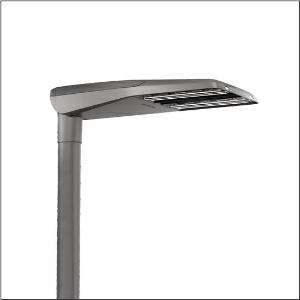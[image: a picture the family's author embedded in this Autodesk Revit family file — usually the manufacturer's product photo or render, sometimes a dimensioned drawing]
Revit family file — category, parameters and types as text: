
# Revit family: streetlight_sl_11_iq_midi___st1_0a_5xc3m41f08le_9450
name_source: partatom
category: Lighting Fixtures
units: mm (PartAtom-declared; Revit-internal decimal feet)

## family parameters
Cut with Voids When Loaded = No
Host = Face
Light Source = No
Part Type = Normal
Room Calculation Point = No
Round Connector Dimension = Use Diameter
Shared = No

## types (1)
- --- (1 x LED, 9290 lm, 60.4 W, 4000K)
    Apparent Load = 60 VA
    CIE Flux Codes = 33 66 96 100 100
    Color Rendering = 70
    Color Temperature = 4000K
    Default Elevation = 1800 mm
    Description = Streetlight SL 11 iQ midi, mast luminaire, primary light control with 3 zone facetted reflector, of plastic, silver coated, highly specular, primary optical cover: cover, of PMMA, transparent, light distribution: ST1.0a, light emission: direct distribution, primary light characteristic: asymmetric, installation type: post-top, side-entry, LED, High Power LED, rated luminous flux: 9.290lm, luminous efficacy: 154lm/W, light colour: 740, colour temperature: 4000K, control: optimised constant luminous flux control (CLO 2.0), Street-Remote, Desk-Remote (wireless, voltage-free reading and setting of iQ features in the workshop via application-optimized NFC function/RFID function), Light-Fading, Smart-Wire, Night-Set, Lumen-Switch, Temp-Guard, Auto-Match, with cable H07RN-F 5x 1.5mm², mains connection: 230..240V, AC, 50/60Hz, connection cable pre-assembled, cable length: 8,5m, start of lifetime: 60W, end of service life: 63W, reduction: 30W, luminaire housing, of diecast aluminium, powder-coated, Siteco® metallic grey (DB 702S), please order mast flange separately, inclination adjustable without tools: 0°, 5°, 10°, 15° (post-top) | 0°, -5°, -10°, -15° (side-entry), sealing non-destructively replaceable, multi-level sealing system, length: 780mm, width: 376mm, height: 118mm, mast flange for spigot size: 42mm (side-entry): 5XC10008XM4, 60/48mm (side-entry/post-top): 5XC10108XM2, 76/60mm (side-entry/post-top): 5XC10108XM1, equipment: standard, protection rating (complete): IP66, insulation class (complete): insulation class II (safety insulation), certification: CE, ENEC, VDE, impact resistance: IK09, permissible operating ambient temperature for outdoor applications: -25..+50°C, standard-compliant lighting for roads and squares, Environmental Product Declaration (EPD) tested and certified by an independent institute, packaging unit: 1 piece

Light Distribution: ST1.0a
    Height = 118 mm
    Lamp = 1 x LED
    Lamp Light Flux = 9290 lm
    Lamp Power = 60.4 W
    Lamp count = 1
    Length = 780 mm
    Luminous efficacy = 154 lm/W
    Manufacturer = Siteco
    ModVariant = No
    Model = 5XC3M41F08LE
    Number of Poles = 1
    OnlyDefault = Yes
    Power Factor = 1
    Product Name = Streetlight SL 11 iQ midi | ST1.0a
    Product group = mast luminaire | pylon top
    ProductGroupID = 6100
    Protection Class = Protection class II
    Protection Degree = IP 66
    RLX_Detail_Level = 1
    RLX_Emergency_Light_Flux = 0 lm
    RLX_Emergency_Type = 0
    RLX_Emergency_Type_DB = No
    RlxData = <blob elided: 70265 chars, md5=83f86bda>
    Socket = socket
    Standby Power = 0 W
    System Light Flux = 9290 lm
    System Power = 60 W
    Type Comments = factory setting: luminous flux: 100 % | dim-lin: 254 | 520 mA
    Type Image = l_1005960.jpg
    URL = http://relux.com
    VarID = @adj_039569
    Voltage = 0 V
    Weight = 0.00 kg
    Width = 376 mm

## geometry (parser evidence)
native form markers: Blend x4, Sweep x11
no freeform markers — native parametric forms only
